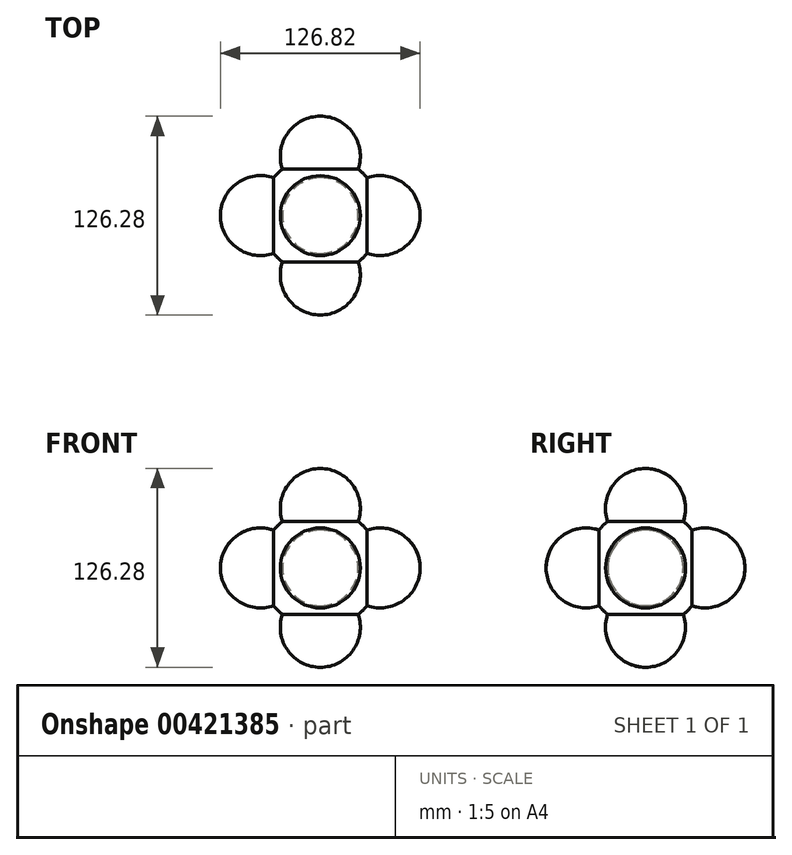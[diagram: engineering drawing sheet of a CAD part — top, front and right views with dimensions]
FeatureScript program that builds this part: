
annotation { "Feature Type Name" : "Feature", "Feature Type Description" : "" }
export const myFeature = defineFeature(function(context is Context, id is Id, definition is map)
    precondition{}
    {
        {
            var Q0;
            Q0=qCreatedBy(makeId("Front.planeOp"),FACE);
            var sketch = newSketch(context, id + "F0", { "sketchPlane" : qUnion([Q0])});
            skArc(sketch, "E0", {"start": v(0, -38.1) * mm, "mid": v(38.1, 0) * mm, "end": v(0, 38.1) * mm});
            skLineSegment(sketch, "E1", {"start": v(0, 38.1) * mm, "end": v(0, -38.1) * mm});
            skSolve(sketch);
        }
        {
            var Q0;
            Q0=makeQuery(id+"F0.imprint","IMPRINT",FACE,{"disambiguationData":[TD([[makeQuery(id+"F0.imprint","IMPRINT",EDGE,{"derivedFrom":sQuery(id+"F0.wireOp",EDGE,"E0")}),1.0]])]});
            var Q1;
            Q1=sQuery(id+"F0.wireOp",EDGE,"E1");
            revolve(context, id + "F1", {"entities" : qUnion([Q0]), "axis" : qUnion([Q1]), "revolveType" : RevolveType.FULL});
        }
        {
            var Q0;
            Q0=qCreatedBy(makeId("Right.planeOp"),FACE);
            var sketch = newSketch(context, id + "F2", { "sketchPlane" : qUnion([Q0])});
            skArc(sketch, "E2", {"start": v(0, 12.34) * mm, "mid": v(25.4, 37.74) * mm, "end": v(0, 63.14) * mm});
            skLineSegment(sketch, "E3", {"start": v(0, 63.14) * mm, "end": v(0, 12.34) * mm});
            skLineSegment(sketch, "E4.1.0", {"start": v(-63.14, 0) * mm, "end": v(-12.34, 0) * mm});
            skArc(sketch, "E4.1.1", {"start": v(-12.34, 0) * mm, "mid": v(-37.74, 25.4) * mm, "end": v(-63.14, 0) * mm});
            skLineSegment(sketch, "E4.2.0", {"start": v(0, -63.14) * mm, "end": v(0, -12.34) * mm});
            skArc(sketch, "E4.2.1", {"start": v(0, -12.34) * mm, "mid": v(-25.4, -37.74) * mm, "end": v(0, -63.14) * mm});
            skPoint(sketch, "E4.center", {"position": v(0, 0) * mm});
            skLineSegment(sketch, "E5.2.3.0", {"start": v(63.14, 0) * mm, "end": v(12.34, 0) * mm});
            skArc(sketch, "E5.3.3.0", {"start": v(12.34, 0) * mm, "mid": v(37.74, -25.4) * mm, "end": v(63.14, 0) * mm});
            skSolve(sketch);
        }
        {
            var Q0;
            Q0=makeQuery(id+"F2.imprint","IMPRINT",FACE,{"disambiguationData":[TD([[makeQuery(id+"F2.imprint","IMPRINT",EDGE,{"derivedFrom":sQuery(id+"F2.wireOp",EDGE,"E2")}),1.0]])]});
            var Q1;
            Q1=sQuery(id+"F2.wireOp",EDGE,"E3");
            revolve(context, id + "F3", {"operationType" : NewBodyOperationType.ADD, "entities" : qUnion([Q0]), "axis" : qUnion([Q1]), "revolveType" : RevolveType.FULL});
        }
        {
            var Q0;
            Q0=makeQuery(id+"F2.imprint","IMPRINT",FACE,{"disambiguationData":[TD([[makeQuery(id+"F2.imprint","IMPRINT",EDGE,{"derivedFrom":sQuery(id+"F2.wireOp",EDGE,"E4.1.0")}),1.0]])]});
            var Q1;
            Q1=sQuery(id+"F2.wireOp",EDGE,"E4.1.0");
            revolve(context, id + "F4", {"operationType" : NewBodyOperationType.ADD, "entities" : qUnion([Q0]), "axis" : qUnion([Q1]), "revolveType" : RevolveType.FULL});
        }
        {
            var Q0;
            Q0=makeQuery(id+"F2.imprint","IMPRINT",FACE,{"disambiguationData":[TD([[makeQuery(id+"F2.imprint","IMPRINT",EDGE,{"derivedFrom":sQuery(id+"F2.wireOp",EDGE,"E4.2.0")}),1.0]])]});
            var Q1;
            Q1=sQuery(id+"F2.wireOp",EDGE,"E4.2.0");
            revolve(context, id + "F5", {"operationType" : NewBodyOperationType.ADD, "entities" : qUnion([Q0]), "axis" : qUnion([Q1]), "revolveType" : RevolveType.FULL});
        }
        {
            var Q0;
            Q0=makeQuery(id+"F2.imprint","IMPRINT",FACE,{"disambiguationData":[TD([[makeQuery(id+"F2.imprint","IMPRINT",EDGE,{"derivedFrom":sQuery(id+"F2.wireOp",EDGE,"E5.2.3.0")}),1.0]])]});
            var Q1;
            Q1=sQuery(id+"F2.wireOp",EDGE,"E5.2.3.0");
            revolve(context, id + "F6", {"operationType" : NewBodyOperationType.ADD, "entities" : qUnion([Q0]), "axis" : qUnion([Q1]), "revolveType" : RevolveType.FULL});
        }
        {
            var Q0;
            Q0=qCreatedBy(makeId("Front.planeOp"),FACE);
            var sketch = newSketch(context, id + "F7", { "sketchPlane" : qUnion([Q0])});
            skArc(sketch, "E6", {"start": v(-12.61, 0) * mm, "mid": v(-38.01, 25.4) * mm, "end": v(-63.41, 0) * mm});
            skLineSegment(sketch, "E7", {"start": v(-63.41, 0) * mm, "end": v(-12.61, 0) * mm});
            skLineSegment(sketch, "E8.MirrorCS", {"start": v(63.41, 0) * mm, "end": v(12.61, 0) * mm});
            skArc(sketch, "E9.MirrorCS", {"start": v(12.61, 0) * mm, "mid": v(38.01, 25.4) * mm, "end": v(63.41, 0) * mm});
            skSolve(sketch);
        }
        {
            var Q0;
            Q0=makeQuery(id+"F7.imprint","IMPRINT",FACE,{"disambiguationData":[TD([[makeQuery(id+"F7.imprint","IMPRINT",EDGE,{"derivedFrom":sQuery(id+"F7.wireOp",EDGE,"E6")}),1.0]])]});
            var Q1;
            Q1=sQuery(id+"F7.wireOp",EDGE,"E7");
            revolve(context, id + "F8", {"operationType" : NewBodyOperationType.ADD, "entities" : qUnion([Q0]), "axis" : qUnion([Q1]), "revolveType" : RevolveType.FULL});
        }
        {
            var Q0;
            Q0=makeQuery(id+"F7.imprint","IMPRINT",FACE,{"disambiguationData":[TD([[makeQuery(id+"F7.imprint","IMPRINT",EDGE,{"derivedFrom":sQuery(id+"F7.wireOp",EDGE,"E8.MirrorCS")}),-1.0]])]});
            var Q1;
            Q1=sQuery(id+"F7.wireOp",EDGE,"E8.MirrorCS");
            revolve(context, id + "F9", {"operationType" : NewBodyOperationType.ADD, "entities" : qUnion([Q0]), "axis" : qUnion([Q1]), "revolveType" : RevolveType.FULL});
        }
    });
